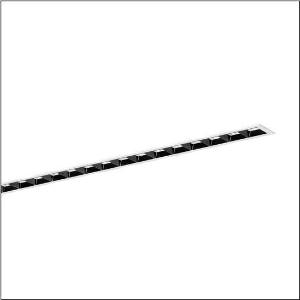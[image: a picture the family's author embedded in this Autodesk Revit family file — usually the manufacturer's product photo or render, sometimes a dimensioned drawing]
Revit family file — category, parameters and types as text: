
# Revit family: silica_r__21_51mx11dc3awb_9b11
name_source: partatom
category: Lighting Fixtures
units: mm (PartAtom-declared; Revit-internal decimal feet)

## family parameters
Cut with Voids When Loaded = No
Host = Face
Light Source = No
Part Type = Normal
Room Calculation Point = No
Round Connector Dimension = Use Diameter
Shared = No

## types (1)
- --- (1 x LED, 10800 lm, 69.3 W, 3000K)
    Apparent Load = 69 VA
    CIE Flux Codes = 87 99 100 100 100
    Color Rendering = 80
    Color Temperature = 3000K
    Default Elevation = 1800 mm
    Description = Silica® 21, office luminaire, primary light control with darklight reflector, of PMMA, black, CAT 2 (L<= 3000cd/m²), light emission: direct distribution, primary light characteristic: symmetric, installation type: recessed, LED, rated luminous flux: 10.800lm, luminous efficacy: 156lm/W, light colour: 830, colour temperature: 3000K, with terminal, 3+2-pole, max. 2.5mm², mains connection: 220..240V, AC, 50/60Hz, luminaire housing, of aluminium, traffic white (RAL 9016), length: 3.028mm, width: 79mm, height: 53mm, protection rating (complete): IP20, insulation class (complete): insulation class I (protective earthing), certification: CE, permissible operating ambient temperature: 0..+35°C, standard: EN 50419, packaging unit: 1 piece
    Height = 0 mm  [stored 0 ft]
    Lamp = 1 x LED
    Lamp Light Flux = 10800 lm
    Lamp Power = 69.3 W
    Lamp count = 1
    Length = 3027 mm
    Luminous efficacy = 156 lm/W
    Manufacturer = Siteco
    ModVariant = No
    Model = 51MX11DC3AWB
    Mounting Place = Ceiling
    Mounting Type = Recessed
    Number of Poles = 1
    OnlyDefault = Yes
    Power Factor = 1
    Product Name = Silica® 21
    Product group = office luminaire | ceiling recessed
    ProductGroupID = 401
    Protection Class = Protection class I
    Protection Degree = IP 20
    RLX_Detail_Level = 1
    RLX_Emergency_Light_Flux = 0 lm
    RLX_Emergency_Type = 0
    RLX_Emergency_Type_DB = No
    RlxData = <blob elided: 62649 chars, md5=ecb6c7d3>
    Socket = socket
    Standby Power = 0 W
    System Light Flux = 10800 lm
    System Power = 69 W
    Type Comments = factory setting: luminous flux: 100 % | dim-lin: 254 | 393 mA
    Type Image = l_1297791.jpg
    URL = http://relux.com
    VarID = @adj_054023
    Voltage = 0 V
    Weight = 0.00 kg
    Width = 79 mm

note: [stored X ft] marks values corroborated as IEEE doubles in the binary element streams (Revit-internal decimal feet)

## geometry (parser evidence)
native form markers: Blend x4, Sweep x10
no freeform markers — native parametric forms only
